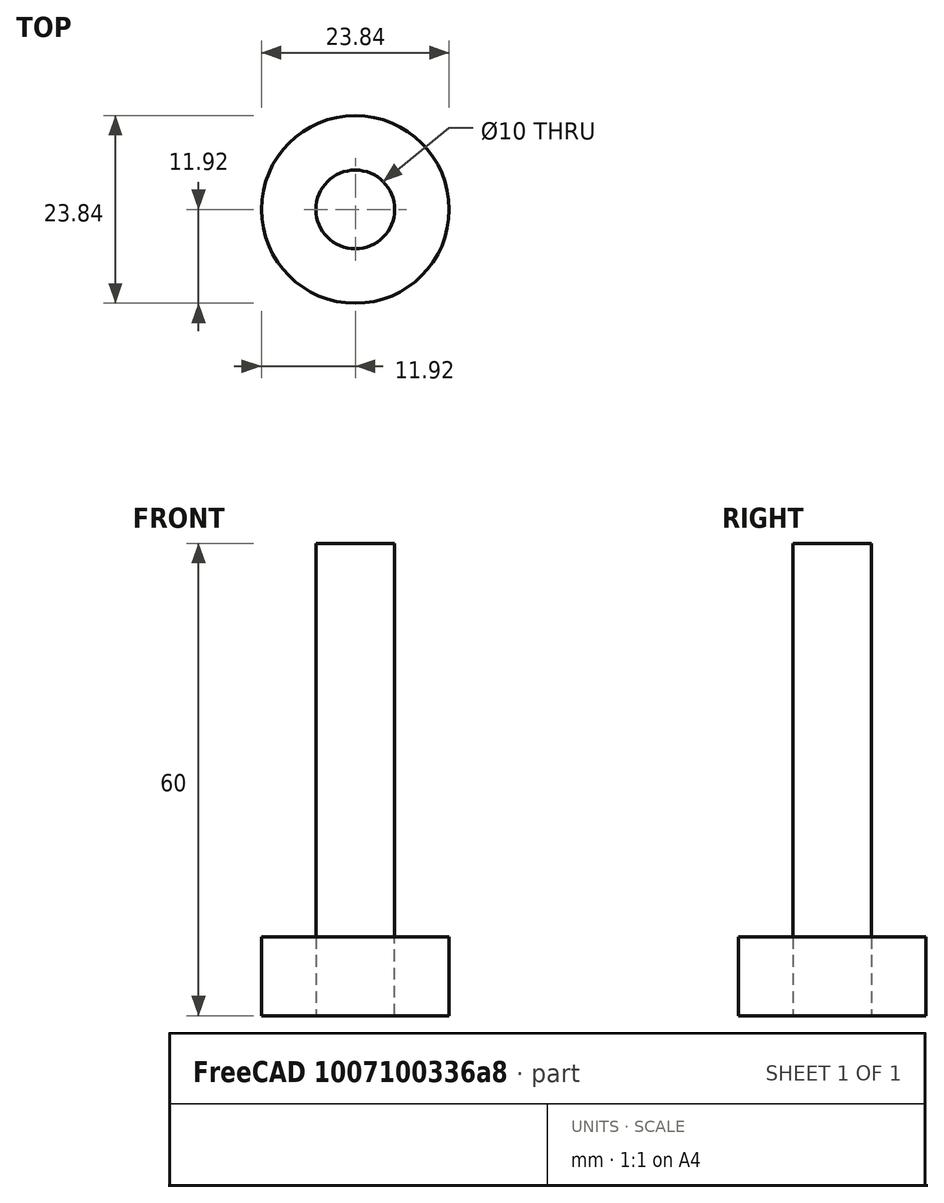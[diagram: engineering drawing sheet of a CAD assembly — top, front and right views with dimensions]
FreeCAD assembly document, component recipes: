
FREECAD ASSEMBLY — COMPONENT RECIPES ("screw")

This assembly document has 2 components, labeled P0..P1 below (a component is one placed body or linked part). 2 of them carry a construction recipe — the FreeCAD feature program that regenerates the part from scratch, quoted from this document or its linked companion documents; the rest are supplied as boundary geometry only. No exploded tour is included for this assembly.
COMPONENT P0 — recipe-attached ("nut001", modeled in this document).
Construction recipe (the document's own serialized feature program — sketch geometry with constraints, then the solid features built on it; lengths are millimeters unless a unit is written):

FEATURE [Sketcher::SketchObject] Sketch
  ArcFitTolerance = 1e-06
  AttachmentSupport = -> [Origin]
  ExternalTypes = [0]
  FullyConstrained = false
  MakeInternals = true
  MapMode = 5
  _ExternalGeoVersion = 1
  sketch-geometry (2):
    g0: Circle CenterX=0 CenterY=0 CenterZ=0 NormalX=0 NormalY=0 NormalZ=1 AngleXU=0 Radius=11.9213
    g1: Circle CenterX=0 CenterY=0 CenterZ=0 NormalX=0 NormalY=0 NormalZ=1 AngleXU=0 Radius=5
  constraints (3):
    c: Coincident(g0,g-1)
    c: Coincident(g1,g0)
    c: Diameter(g1) = 10
FEATURE [PartDesign::Pad] Pad
  Direction = (0,0,1)
  Length = 10
  Length2 = 10
  Profile = -> Sketch
  ReferenceAxis = -> Sketch [N_Axis]
  Refine = true
  SideType = 0
  Suppressed = false
  Type = 0
  Type2 = 0
FEATURE [PartDesign::Body] Body  label="nut"
  AllowCompound = true
  Group = -> [Sketch,Pad]
  Origin = -> Origin
  Tip = -> Pad
COMPONENT P1 — recipe-attached ("screw001", modeled in this document).
Construction recipe (the document's own serialized feature program — sketch geometry with constraints, then the solid features built on it; lengths are millimeters unless a unit is written):

FEATURE [Sketcher::SketchObject] Sketch001
  ArcFitTolerance = 1e-06
  AttachmentSupport = -> [Origin002]
  ExternalTypes = [0]
  FullyConstrained = true
  MakeInternals = true
  MapMode = 5
  _ExternalGeoVersion = 1
  sketch-geometry (1):
    g0: Circle CenterX=0 CenterY=0 CenterZ=0 NormalX=0 NormalY=0 NormalZ=1 AngleXU=0 Radius=5
  constraints (2):
    c: Coincident(g0,g-1)
    c: Diameter(g0) = 10
FEATURE [PartDesign::Pad] Pad001
  Direction = (0,0,1)
  Length = 60
  Length2 = 10
  Profile = -> Sketch001
  ReferenceAxis = -> Sketch001 [N_Axis]
  Refine = true
  SideType = 0
  Suppressed = false
  Type = 0
  Type2 = 0
FEATURE [PartDesign::Body] Body001  label="screw"
  AllowCompound = true
  Group = -> [Sketch001,Pad001]
  Origin = -> Origin002
  Tip = -> Pad001
PROVENANCE & LICENSES
A FreeCAD (.FCStd) document from a public repository crawl; recipes are the document's own serialized feature recipes (and, for linked parts, companion documents' recipes).
License: as declared in the source repository (recorded in the dataset sidecar).
